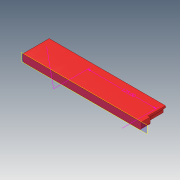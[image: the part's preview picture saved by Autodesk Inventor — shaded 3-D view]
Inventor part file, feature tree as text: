
AUTODESK INVENTOR PART (.ipt)
format: ipt  version: 2019 (Build 230136000, 136)  size: 261,632 bytes
history: native  units: mm
features: extrude x11, sketch x10, plane x4, projected_geometry x3, other x2, fillet x2
ambient origin geometry x8: Origin, YZ Plane, XZ Plane, XY Plane, X Axis, Y Axis, Z Axis, Center Point
bodies: Solid1 (feature_tree)
feature tree (32):
  other  "Annotations"
  extrude  "Extrusion1"  Depth=135.0mm
  extrude  "Extrusion2"  Depth=5.0mm
  extrude  "Extrusion3"  Depth=3.0mm TaperAngle=0.0deg
  sketch  "Sketch6"  dims[d9=3.0mm d10=20.0mm d11=0.0mm]
  fillet  "Fillet1"  Radius=3.0mm
  plane  "Work Plane4"
  extrude  "Extrusion8"  Depth=20.0mm TaperAngle=0.0deg
  extrude  "Extrusion9"  Depth=2.5mm TaperAngle=0.0deg
  fillet  "Fillet4"  Radius=35.0mm
  extrude  "Extrusion10"  Depth=16.0mm
  plane  "Work Plane5"
  extrude  "Extrusion11"  TaperAngle=0.0deg  [1 undecoded]
  plane  "Work Plane3"
  extrude  "Extrusion13"  Depth=40.0mm
  extrude  "Extrusion14"  Depth=16.0mm TaperAngle=0.0deg
  extrude  "Extrusion15"  Depth=125.0mm
  plane  "Work Plane6"
  extrude  "Extrusion16"  Depth=6.0mm
  sketch  "Sketch1"  dims[d0=135.0mm d1=150.0mm]
  sketch  "Sketch3"  dims[d2=8.0mm d3=0.0mm d4=5.0mm]
  projected_geometry  "Projected Loop2"
  sketch  "Sketch4"  dims[d5=5.0mm d6=38.7mm d7=0.0mm d8=3.0mm]
  projected_geometry  "Projected Loop3"
  sketch  "Sketch15"  dims[d25=2.0mm d37=2.5mm d38=0.0mm d39=35.0mm]
  projected_geometry  "Projected Loop7"
  sketch  "Sketch16"  dims[d40=0.0mm d41=16.0mm]
  sketch  "Sketch17"  dims[d42=40.0mm d43=0.0mm]
  sketch  "Sketch21"  dims[d44=0.0mm d45=40.0mm]
  sketch  "Sketch22"  dims[d46=16.0mm d47=16.0mm d48=0.0mm]
  sketch  "Sketch23"  dims[d49=1.0mm d50=4.5mm d51=6.0mm d52=9.0mm d53=4.5mm d54=7.0mm d56=12.0mm d57=0.0mm d60=4.5mm d61=4.5mm d62=30.8mm d65=0.0mm d66=0.0mm d67=100.0mm d76=-1.5mm d78=7.5mm d79=7.5mm d80=3.15mm d81=0.0mm d90=12.5mm d91=18.0mm d92=13.0mm d93=17.0mm d94=12.0mm d95=10.0mm d96=0.0mm d97=0.0mm d98=0.0mm d99=-10.0mm d100=0.0mm d101=0.0mm d73=4.870635mm d74=1.41766mm d75=125.0mm]
  other  "Linear Dimension 1"
note: 1 required parameter value undecoded (feature->parameter linkage not recoverable at this tier; creation-order binding heuristic only, values carry confidence <= 0.55)
